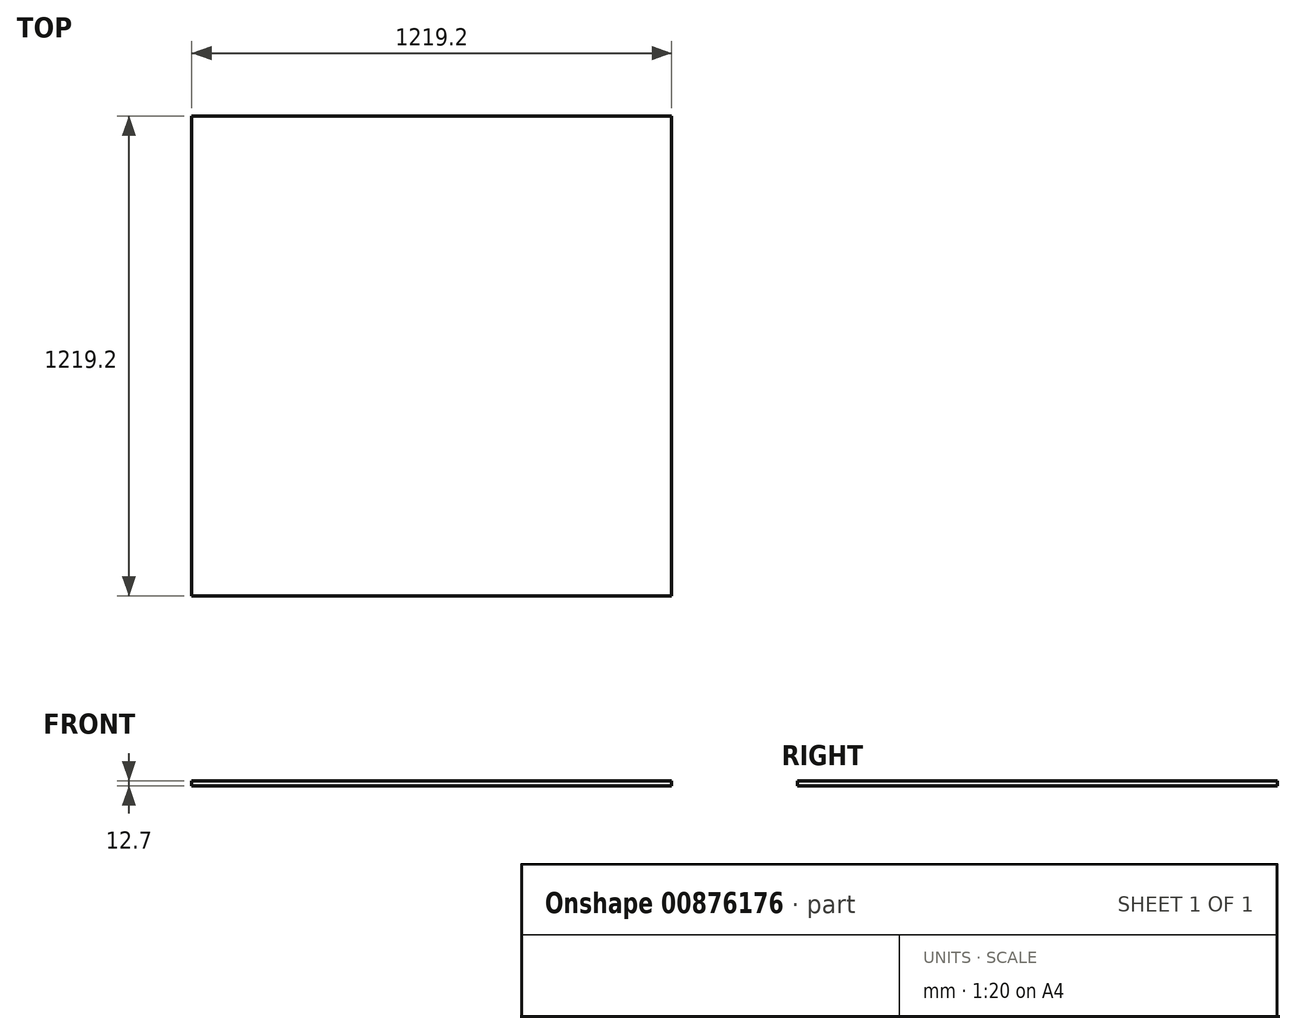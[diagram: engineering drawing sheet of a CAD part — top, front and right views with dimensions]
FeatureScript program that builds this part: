
annotation { "Feature Type Name" : "Feature", "Feature Type Description" : "" }
export const myFeature = defineFeature(function(context is Context, id is Id, definition is map)
    precondition{}
    {
        {
            var Q0;
            Q0=qCreatedBy(makeId("Top.planeOp"),FACE);
            var sketch = newSketch(context, id + "F0", { "sketchPlane" : qUnion([Q0])});
            skLineSegment(sketch, "E0.bottom", {"start": v(-600.5, 682.85) * mm, "end": v(618.7, 682.85) * mm});
            skLineSegment(sketch, "E0.top", {"start": v(-600.5, -536.35) * mm, "end": v(618.7, -536.35) * mm});
            skLineSegment(sketch, "E0.left", {"start": v(-600.5, 682.85) * mm, "end": v(-600.5, -536.35) * mm});
            skLineSegment(sketch, "E0.right", {"start": v(618.7, 682.85) * mm, "end": v(618.7, -536.35) * mm});
            skSolve(sketch);
        }
        {
            var Q0;
            Q0=qSketchRegion(id+"F0",true);
            extrude(context, id + "F1", {"entities" : qUnion([Q0]), "depth" : 12.7 * mm, "offsetDistance" : 25.4 * mm});
        }
    });
